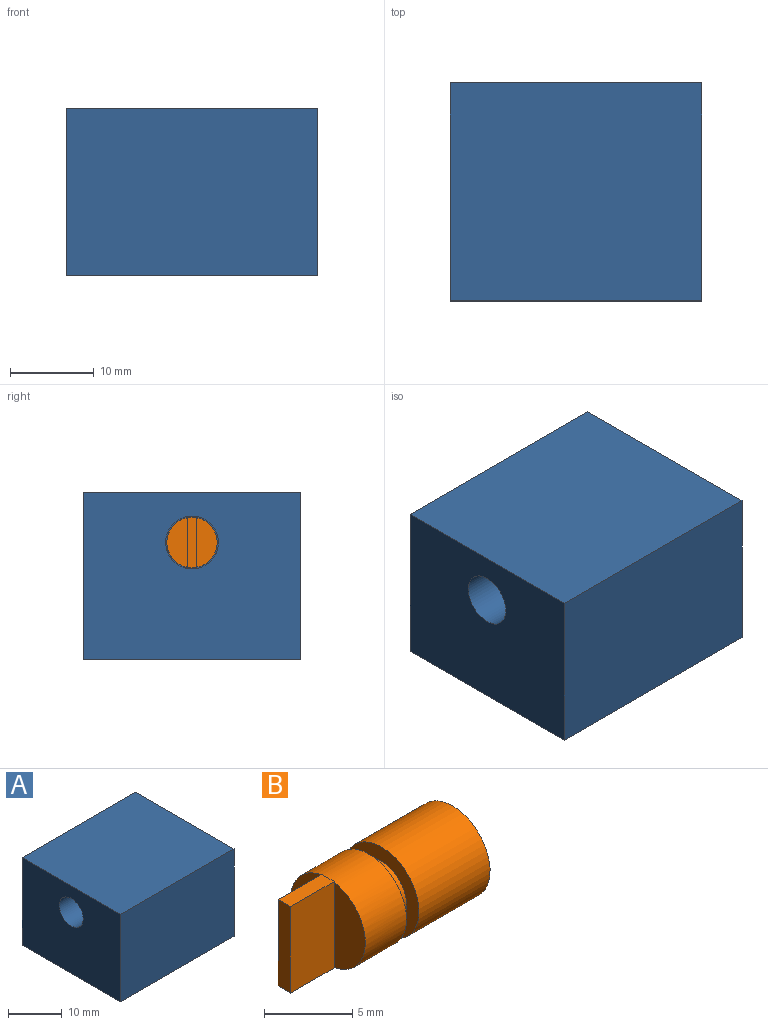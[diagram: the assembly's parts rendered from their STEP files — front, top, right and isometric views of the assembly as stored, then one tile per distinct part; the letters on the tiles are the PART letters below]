
ASSEMBLY  parts=2 mates=1
PART A: 9 faces, bbox 30x26x20 mm
  f0: plane 26x20mm, normal (-1,0,0), area 488.8mm2, adj f1,f3,f4,f5,f7
  f1: plane 30x20mm, normal (0,-1,0), area 600mm2, adj f0,f2,f4,f5
  f2: plane 26x20mm, normal (1,0,0), area 508.7mm2, adj f1,f3,f4,f5,f8
  f3: plane 30x20mm, normal (0,1,0), area 600mm2, adj f0,f2,f4,f5
  f4: plane 30x26mm, normal (0,0,1), area 780mm2, adj f0,f1,f2,f3
  f5: plane 30x26mm, normal (0,0,-1), area 780mm2, adj f0,f1,f2,f3
  f6: plane 6.3x6.3mm, normal (-1,0,0), area 19.8mm2, adj f7,f8
  f7: cylinder r=3.15mm len=25mm, axis (-1,0,0), area 494.8mm2, adj f0,f6
  f8: cylinder r=1.9mm len=5mm, axis (-1,0,0), area 59.7mm2, adj f2,f6
PART B: 19 faces, bbox 13.5x6x6 mm
  f0: plane 5.92x2.5mm, normal (-1,0,0), area 11.2mm2, adj f5,f17
  f1: cylinder r=3mm len=6mm, axis (-1,0,0), area 107.4mm2, adj f2,f3
  f2: plane 6x6mm, normal (1,0,0), area 22.6mm2, adj f1,f8
  f3: plane 6x6mm, normal (-1,0,0), area 15.7mm2, adj f1,f4
  f4: cylinder r=2mm len=4mm, axis (1,0,0), area 12.6mm2, adj f3,f7
  f5: cylinder r=3mm len=6mm, axis (1,0,0), area 62.2mm2, adj f0,f6,f7,f10,f11,f12,f13
  f6: plane 5.92x2.5mm, normal (-1,0,0), area 11.2mm2, adj f5,f15
  f7: plane 6x6mm, normal (1,0,0), area 15.7mm2, adj f4,f5
  f8: cylinder r=1.34mm len=2.68mm, axis (1,0,0), area 8.4mm2, adj f2,f9
  f9: plane 2.68x2.68mm, normal (1,0,0), area 5.7mm2, adj f8
  f10: plane 0.5x0.04mm, normal (1,0,0), area 0mm2, adj f5,f14,f17
  f11: plane 0.5x0.04mm, normal (1,0,0), area 0mm2, adj f5,f14,f15
  f12: plane 0.5x0.04mm, normal (1,0,0), area 0mm2, adj f5,f15,f16
  f13: plane 0.5x0.04mm, normal (1,0,0), area 0mm2, adj f5,f16,f17
  f14: plane 3.5x1mm, normal (0,0,1), area 3.5mm2, adj f10,f11,f15,f17,f18
  f15: plane 6x3.5mm, normal (0,1,0), area 21mm2, adj f6,f11,f12,f14,f16,f18
  f16: plane 3.5x1mm, normal (0,0,-1), area 3.5mm2, adj f12,f13,f15,f17,f18
  f17: plane 6x3.5mm, normal (0,-1,0), area 21mm2, adj f0,f10,f13,f14,f16,f18
  f18: plane 6x1mm, normal (-1,0,0), area 6mm2, adj f14,f15,f16,f17
PLACE A at identity fixed
PLACE B t=(19.2,-13,14)mm
MATE slider A.f7 <-> B.f1  axis (-1,0,0) through (0,-13,14)mm
